# Revit family: WCPan-WallHung-55cm-Vitra-PluralSeries-7830
name_source: partatom
category: Plumbing Fixtures
revit_build: Autodesk Revit 2017 (Build: 20160225_1515(x64)
units: mm (PartAtom-declared; Revit-internal decimal feet)

## family parameters
Cut with Voids When Loaded = No
Host = Face
OmniClass Number = 23.45.05.21.11
OmniClass Title = Water Closets
Part Type = Normal
Room Calculation Point = No
Round Connector Dimension = Use Diameter
Shared = Yes

## types (20) — shared parameters
BIMobject category = Sanitary - Toilets
Brand = VitrA
CW Connection = Yes
Default Elevation = 410 mm  [stored 1.34514 ft]
Description = VitrA Plural Wall Mounted WC
Design country = Turkey
HW Connection = No
IFC Classification = Sanitary Terminal
Main Material = Ceramic
Manufacturer = Vitra
Manufacturer name = VitrA
Masterformat 2014 Code = 22 45 26
Masterformat 2014 Description = Sanitary Facilities
Mounting type = Wall Hung
NBS Referans Code = 35-65-90
NBS Referans Description = Toilet Systems
Nominal Depth (mm) = 548 mm  [stored 1.7979 ft]
Nominal Height (mm) = 340 mm  [stored 1.11549 ft]
Nominal Width (mm) = 360 mm  [stored 1.1811 ft]
OmniClass Code = 23-31 19 00
OmniClass Description = Toilets
Primary Material = <By Category>
Product certification = https://www.vitraglobal.com
Product family = Plural
Product group = Wall Mounted WC
UNSPSC Code = 301815
UNSPSC Description = Sanitary Ware
URL = https://www.vitraglobal.com
Uniclass 1.4 Code = L7216
Uniclass 1.4 Description = Toilets
Uniclass 2.0 Code = SS-35-65-90
Uniclass 2.0 Description = Toilet Systems
Uniclass 2015 Code = Pr_40_20_93
Uniclass 2015 Name = Urinal and WC fittings
Uniformat II Code = D2010
Uniformat II Description = Sanitary Facilities
Vent Connection = No
Warranty Period (Year) = 10 Years
Waste Connection = Yes
Weight Net (kg) = 28.4
Youtube = https://www.youtube.com

## per-type parameters (varying)
| type | Article No. (default) | Color | Model | Product SKU | Product data url | Product url | Secondary Material | Technical description |
| WC_WallMountedWC_Vitra_Plural_(MatteMink)_7830B450-0075 | 7830B450-0075 | Matte Mink | 7830B450-0075 | 7830B450-0075 | https://www.vitraglobal.com |  | MatteMink | https://www.vitraglobal.com |
| WC_WallMountedWC_Vitra_Plural_(MatteBlack)_7830B483-0075 | 7830B483-0075 | Matte Black | 7830B483-0075 | 7830B483-0075 | https://www.vitraglobal.com |  | MatteBlack | https://www.vitraglobal.com |
| WC_WallMountedWC_Vitra_Plural_(MatteBeige)_7830B420-0075 | 7830B420-0075 | Matte Beige | 7830B420-0075 | 7830B420-0075 | https://www.vitraglobal.com |  | MatteBeige | https://www.vitraglobal.com |
| WC_WallMountedWC_Vitra_Plural_(White)_7830B403-0075 | 7830B403-0075 | White | 7830B403-0075 | 7830B403-0075 | https://www.bimobject.com | https://www.vitraglobal.com | White | https://www.vitraglobal.com |
| WC_WallMountedWC_Vitra_Plural_(MatteWhite)_7830B401-0075 | 7830B401-0075 | Matte White | 7830B401-0075 | 7830B401-0075 | https://www.vitraglobal.com |  | MatteWhite | https://www.vitraglobal.com |
| WC_WallMountedWC_Vitra_Plural_(MatteBlack)_7830B483-0090 | 7830B483-0090 | Matte Black | 7830B483-0090 | 7830B483-0090 | https://www.vitra.com.tr |  | MatteBlack | https://www.vitra.com.tr |
| WC_WallMountedWC_Vitra_Plural_(MatteMink)_7830B450-0090 | 7830B450-0090 | Matte Mink | 7830B450-0090 | 7830B450-0090 | https://www.vitra.com.tr |  | MatteMink | https://www.vitra.com.tr |
| WC_WallMountedWC_Vitra_Plural_(MatteBeige)_7830B420-0090 | 7830B420-0090 | Matte Beige | 7830B420-0090 | 7830B420-0090 | https://www.vitra.com.tr |  | MatteBeige | https://www.vitra.com.tr |
| WC_WallMountedWC_Vitra_Plural_(MatteWhite)_7830B401-0090 | 7830B401-0090 | Matte White | 7830B401-0090 | 7830B401-0090 | https://www.vitra.com.tr |  | MatteWhite | https://www.vitra.com.tr |
| WC_WallMountedWC_Vitra_Plural_(White)_7830B403-0090 | 7830B403-0090 | White | 7830B403-0090 | 7830B403-0090 | https://www.vitra.com.tr |  | White | https://www.vitra.com.tr |
| WC_WallMountedWC_Vitra_Plural_(MatteWhite)_7830B401H0075 | 7830B401H0075 | Matte White | 7830B401H0075 | 7830B401H0075 |  | https://www.vitra-india.com | MatteWhite | https://www.vitra-india.com |
| WC_WallMountedWC_Vitra_Plural_(MatteWhite)_7830B401H0090 | 7830B401H0090 | Matte White | 7830B401H0090 | 7830B401H0090 |  | https://www.vitra-india.com | MatteWhite | https://www.vitra-india.com |
| WC_WallMountedWC_Vitra_Plural_(White)_7830B403H0075 | 7830B403H0075 | White | 7830B403H0075 | 7830B403H0075 | https://www.bimobject.com | https://www.vitra-india.com | White | https://www.vitra-india.com |
| WC_WallMountedWC_Vitra_Plural_(White)_7830B403H0090 | 7830B403H0090 | White | 7830B403H0090 | 7830B403H0090 |  | https://www.vitra-india.com | White | https://www.vitra-india.com |
| WC_WallMountedWC_Vitra_Plural_(MatteBeige)_7830B420H0075 | 7830B420H0075 | Matte Beige | 7830B420H0075 | 7830B420H0075 |  | https://www.vitra-india.com | MatteBeige | https://www.vitra-india.com |
| WC_WallMountedWC_Vitra_Plural_(MatteBeige)_7830B420H0090 | 7830B420H0090 | Matte Beige | 7830B420H0090 | 7830B420H0090 |  | https://www.vitra-india.com | MatteBeige | https://www.vitra-india.com |
| WC_WallMountedWC_Vitra_Plural_(MatteMink)_7830B450H0075 | 7830B450H0075 | Matte Mink | 7830B450H0075 | 7830B450H0075 |  | https://www.vitra-india.com | MatteMink | https://www.vitra-india.com |
| WC_WallMountedWC_Vitra_Plural_(MatteMink)_7830B450H0090 | 7830B450H0090 | Matte Mink | 7830B450H0090 | 7830B450H0090 |  | https://www.vitra-india.com | MatteMink | https://www.vitra-india.com |
| WC_WallMountedWC_Vitra_Plural_(MatteBlack)_7830B483H0075 | 7830B483H0075 | Matte Black | 7830B483H0075 | 7830B483H0075 |  | https://www.vitra-india.com | MatteBlack | https://www.vitra-india.com |
| WC_WallMountedWC_Vitra_Plural_(MatteBlack)_7830B483H0090 | 7830B483H0090 | Matte Black | 7830B483H0090 | 7830B483H0090 |  | https://www.vitra-india.com | MatteBlack | https://www.vitra-india.com |

note: [stored X ft] marks values corroborated as IEEE doubles in the binary element streams (Revit-internal decimal feet)

## geometry (parser evidence)
native form markers: Sweep x1
no freeform markers — native parametric forms only
